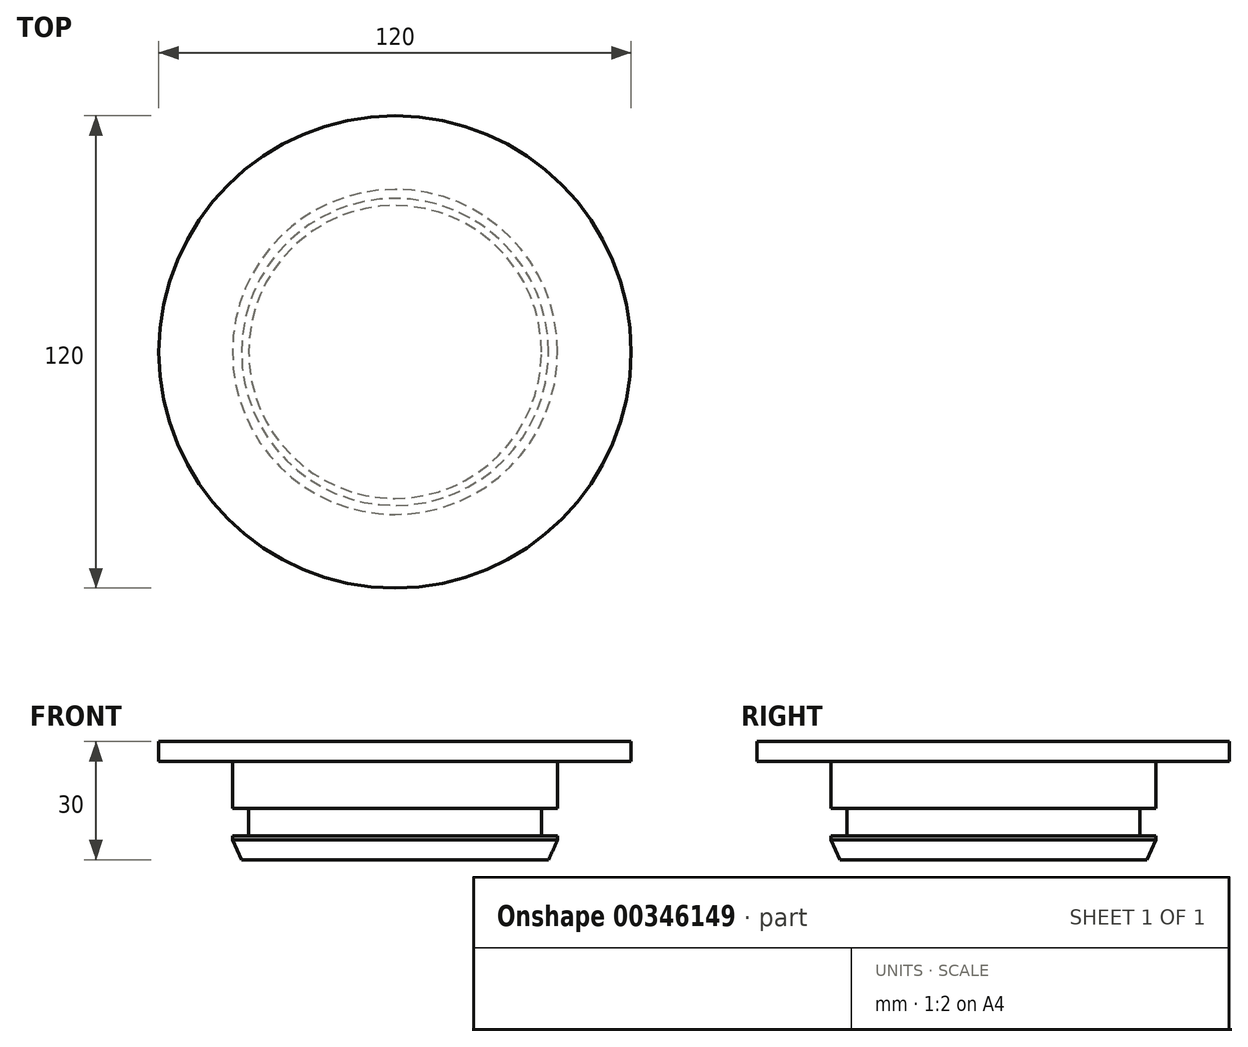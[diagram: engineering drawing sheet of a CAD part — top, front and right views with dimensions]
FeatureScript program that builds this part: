
annotation { "Feature Type Name" : "Feature", "Feature Type Description" : "" }
export const myFeature = defineFeature(function(context is Context, id is Id, definition is map)
    precondition{}
    {
        {
            var Q0;
            Q0=qCreatedBy(makeId("Front.planeOp"),FACE);
            var sketch = newSketch(context, id + "F0", { "sketchPlane" : qUnion([Q0])});
            skPoint(sketch, "E0.end.orphan", {"position": v(50, 0) * mm});
            skPoint(sketch, "E1.orphan", {"position": v(49.6, -21.9) * mm});
            skPoint(sketch, "E2.start.orphan", {"position": v(-24.8, -26.55) * mm});
            skPoint(sketch, "E3.orphan", {"position": v(0, -25) * mm});
            skPoint(sketch, "E4.orphan", {"position": v(-0.05, 0) * mm});
            skPoint(sketch, "E5.orphan", {"position": v(-49.6, -28.1) * mm});
            skPoint(sketch, "E6.visualSharp", {"position": v(-41.65, -21.5) * mm});
            skPoint(sketch, "E7.trimOffspring.start.orphan", {"position": v(-0.1, 0) * mm});
            skPoint(sketch, "E8.orphan", {"position": v(0, -7) * mm});
            skPoint(sketch, "E9.endSnap0", {"position": v(0, -12.5) * mm});
            skLineSegment(sketch, "E10", {"start": v(0, -12) * mm, "end": v(0, -12.5) * mm});
            skPoint(sketch, "E11.start.orphan", {"position": v(-8.5, -7) * mm});
            skLineSegment(sketch, "E12", {"start": v(0, 0) * mm, "end": v(0, -25) * mm});
            skLineSegment(sketch, "E13", {"start": v(-39, -25) * mm, "end": v(0, -25) * mm});
            skLineSegment(sketch, "E14", {"start": v(-41.3, -20) * mm, "end": v(-39, -25) * mm});
            skLineSegment(sketch, "E15", {"start": v(-60, 0) * mm, "end": v(-60, 5) * mm});
            skLineSegment(sketch, "E16", {"start": v(-60, 5) * mm, "end": v(0, 5) * mm});
            skLineSegment(sketch, "E17", {"start": v(0, 5) * mm, "end": v(0, 0) * mm});
            skLineSegment(sketch, "E18", {"start": v(-47.5, 0) * mm, "end": v(-47.5, 0) * mm});
            skLineSegment(sketch, "E19", {"start": v(-60, 0) * mm, "end": v(-0.05, 0) * mm});
            skLineSegment(sketch, "E20", {"start": v(-47.5, 0) * mm, "end": v(-0.05, 0) * mm});
            skLineSegment(sketch, "E21", {"start": v(-41.3, -20) * mm, "end": v(-41.3, -19) * mm});
            skLineSegment(sketch, "E22", {"start": v(0, -12) * mm, "end": v(-42, -12) * mm, "construction": true});
            skLineSegment(sketch, "E23", {"start": v(-42, -12) * mm, "end": v(-37.2, -12) * mm});
            skLineSegment(sketch, "E24", {"start": v(-37.2, -12) * mm, "end": v(-37.2, -19) * mm});
            skLineSegment(sketch, "E25", {"start": v(-37.2, -19) * mm, "end": v(-42, -19) * mm});
            skLineSegment(sketch, "E26.trimOffspring", {"start": v(-41.3, -12) * mm, "end": v(-41.3, 0) * mm});
            skSolve(sketch);
        }
        {
            var Q0;
            Q0=makeQuery(id+"F0.imprint","IMPRINT",FACE,{"disambiguationData":[TD([[makeQuery(id+"F0.imprint","IMPRINT",EDGE,{"derivedFrom":sQuery(id+"F0.wireOp",EDGE,"tUwDb1r3-CcyY-ElWk-cTJ0-fQwOYXJGEc09")}),1.0]])]});
            var Q1;
            {var subQ0=sQuery(id+"F0.wireOp",EDGE,"E13");Q1=makeQuery(id+"F0.imprint","IMPRINT",FACE,{"disambiguationData":[TD([[makeQuery(id+"F0.imprint","IMPRINT",EDGE,{"derivedFrom":subQ0}),1.0]])]});}
            var Q2;
            {var subQ1=sQuery(id+"F0.wireOp",EDGE,"gKxNwJeo-vbOz-fFNv-kCEf-ZZWGcgaghtaw");Q2=makeQuery(id+"F0.imprint","IMPRINT",FACE,{"disambiguationData":[TD([[makeQuery(id+"F0.imprint","IMPRINT",EDGE,{"derivedFrom":subQ1}),1.0]])]});}
            var Q3;
            Q3=sQuery(id+"F0.wireOp",EDGE,"E12");
            revolve(context, id + "F1", {"surfaceOperationType" : NewSurfaceOperationType.NEW, "entities" : qUnion([Q0, Q1, Q2]), "axis" : qUnion([Q3]), "revolveType" : RevolveType.FULL});
        }
    });
